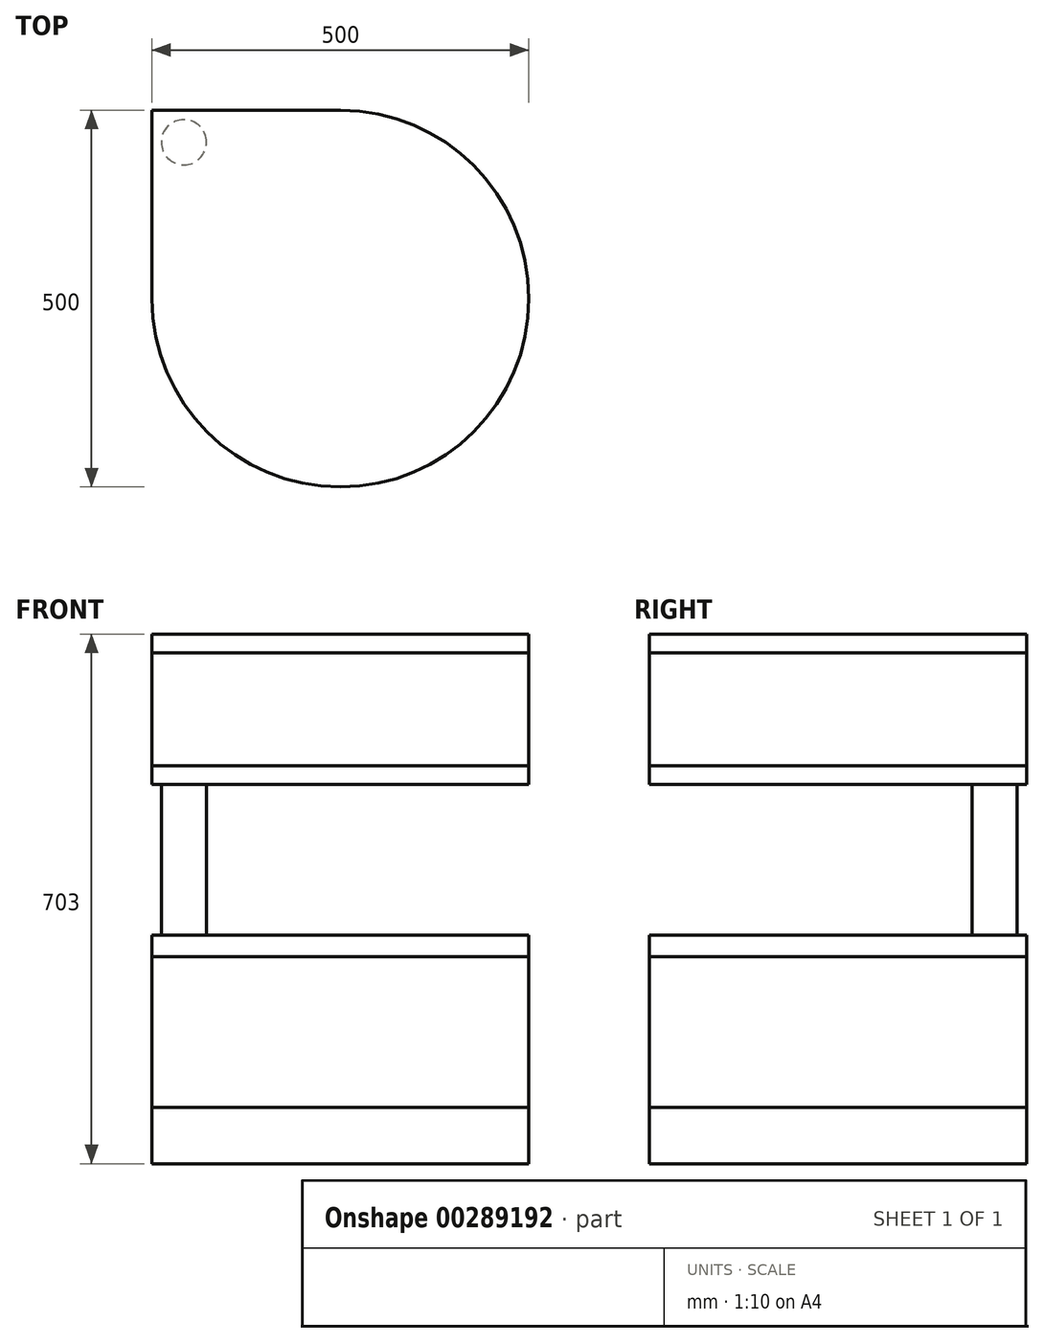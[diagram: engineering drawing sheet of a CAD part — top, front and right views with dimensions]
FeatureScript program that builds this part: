
annotation { "Feature Type Name" : "Feature", "Feature Type Description" : "" }
export const myFeature = defineFeature(function(context is Context, id is Id, definition is map)
    precondition{}
    {
        {
            var Q0;
            Q0=qCreatedBy(makeId("Top.planeOp"),FACE);
            var sketch = newSketch(context, id + "F0", { "sketchPlane" : qUnion([Q0])});
            skArc(sketch, "E0", {"start": v(-142.68, -107.32) * mm, "mid": v(284.1, -284.1) * mm, "end": v(107.32, 142.68) * mm});
            skLineSegment(sketch, "E1", {"start": v(-142.68, -107.32) * mm, "end": v(-142.68, 142.68) * mm});
            skLineSegment(sketch, "E2", {"start": v(-142.68, 142.68) * mm, "end": v(107.32, 142.68) * mm});
            skSolve(sketch);
        }
        {
            var Q0;
            Q0=makeQuery(id+"F0.imprint","IMPRINT",FACE,{"disambiguationData":[TD([[makeQuery(id+"F0.imprint","IMPRINT",EDGE,{"derivedFrom":sQuery(id+"F0.wireOp",EDGE,"E0")}),1.0]])]});
            extrude(context, id + "F1", {"entities" : qUnion([Q0]), "depth" : 75 * mm});
        }
        {
            var Q0;
            Q0=makeQuery(id+"F1.opExtrude","CAP_FACE",FACE,{"disambiguationData":[OSD([sQuery(id+"F0.wireOp",EDGE,"E0"),sQuery(id+"F0.wireOp",EDGE,"E1"),sQuery(id+"F0.wireOp",EDGE,"E2")])],"isStart":false});
            extrude(context, id + "F2", {"entities" : qUnion([Q0]), "depth" : 200 * mm});
        }
        {
            var Q0;
            Q0=makeQuery(id+"F2.opExtrude","CAP_FACE",FACE,{"disambiguationData":[OSD([sQuery(id+"F0.wireOp",EDGE,"E0"),sQuery(id+"F0.wireOp",EDGE,"E1"),sQuery(id+"F0.wireOp",EDGE,"E2")])],"isStart":false});
            extrude(context, id + "F3", {"entities" : qUnion([Q0]), "depth" : 3 * mm});
        }
        {
            var Q0;
            Q0=makeQuery(id+"F3.opExtrude","CAP_FACE",FACE,{"disambiguationData":[OSD([sQuery(id+"F0.wireOp",EDGE,"E0"),sQuery(id+"F0.wireOp",EDGE,"E1"),sQuery(id+"F0.wireOp",EDGE,"E2")])],"isStart":false});
            extrude(context, id + "F4", {"entities" : qUnion([Q0]), "operationType" : NewBodyOperationType.ADD, "depth" : 25 * mm});
        }
        {
            var Q0;
            Q0=makeQuery(id+"F4.opExtrude","CAP_FACE",FACE,{"disambiguationData":[OSD([sQuery(id+"F0.wireOp",EDGE,"E0"),sQuery(id+"F0.wireOp",EDGE,"E1"),sQuery(id+"F0.wireOp",EDGE,"E2")])],"isStart":false});
            extrude(context, id + "F5", {"entities" : qUnion([Q0]), "depth" : 225 * mm, "hasSecondDirection" : true, "secondDirectionOppositeDirection" : false, "secondDirectionDepth" : 200 * mm});
        }
        {
            var Q0;
            Q0=makeQuery(id+"F5.opExtrude","CAP_FACE",FACE,{"disambiguationData":[OSD([sQuery(id+"F0.wireOp",EDGE,"E0"),sQuery(id+"F0.wireOp",EDGE,"E1"),sQuery(id+"F0.wireOp",EDGE,"E2")])],"isStart":false});
            extrude(context, id + "F6", {"entities" : qUnion([Q0]), "depth" : 150 * mm});
        }
        {
            var Q0;
            Q0=makeQuery(id+"F6.opExtrude","CAP_FACE",FACE,{"disambiguationData":[OSD([sQuery(id+"F0.wireOp",EDGE,"E0"),sQuery(id+"F0.wireOp",EDGE,"E1"),sQuery(id+"F0.wireOp",EDGE,"E2")])],"isStart":false});
            extrude(context, id + "F7", {"entities" : qUnion([Q0]), "depth" : 25 * mm});
        }
        {
            var Q0;
            Q0=makeQuery(id+"F4.opExtrude","CAP_FACE",FACE,{"disambiguationData":[OSD([sQuery(id+"F0.wireOp",EDGE,"E0"),sQuery(id+"F0.wireOp",EDGE,"E1"),sQuery(id+"F0.wireOp",EDGE,"E2")])],"isStart":false});
            var sketch = newSketch(context, id + "F8", { "sketchPlane" : qUnion([Q0])});
            skLineSegment(sketch, "E3", {"start": v(-142.68, -107.32) * mm, "end": v(107.32, 142.68) * mm, "construction": true});
            skLineSegment(sketch, "E4", {"start": v(-142.68, 142.68) * mm, "end": v(-17.68, 17.68) * mm, "construction": true});
            skCircle(sketch, "E5", {"center": v(-100.26, 100.26) * mm, "radius": 30 * mm});
            skCircle(sketch, "E6", {"center": v(107.32, -107.32) * mm, "radius": 250 * mm, "construction": true});
            skPoint(sketch, "E6.first.point", {"position": v(-26.23, -318.66) * mm});
            skPoint(sketch, "E6.second.point", {"position": v(316.4, 29.75) * mm});
            skPoint(sketch, "E6.third.point", {"position": v(175.29, 133.27) * mm});
            skSolve(sketch);
        }
        {
            var Q0;
            Q0=makeQuery(id+"F8.imprint","IMPRINT",FACE,{"disambiguationData":[TD([[makeQuery(id+"F8.imprint","IMPRINT",EDGE,{"derivedFrom":sQuery(id+"F8.wireOp",EDGE,"E5")}),1.0]])]});
            extrude(context, id + "F9", {"entities" : qUnion([Q0]), "endBound" : BoundingType.UP_TO_NEXT, "depth" : 25 * mm});
        }
    });
